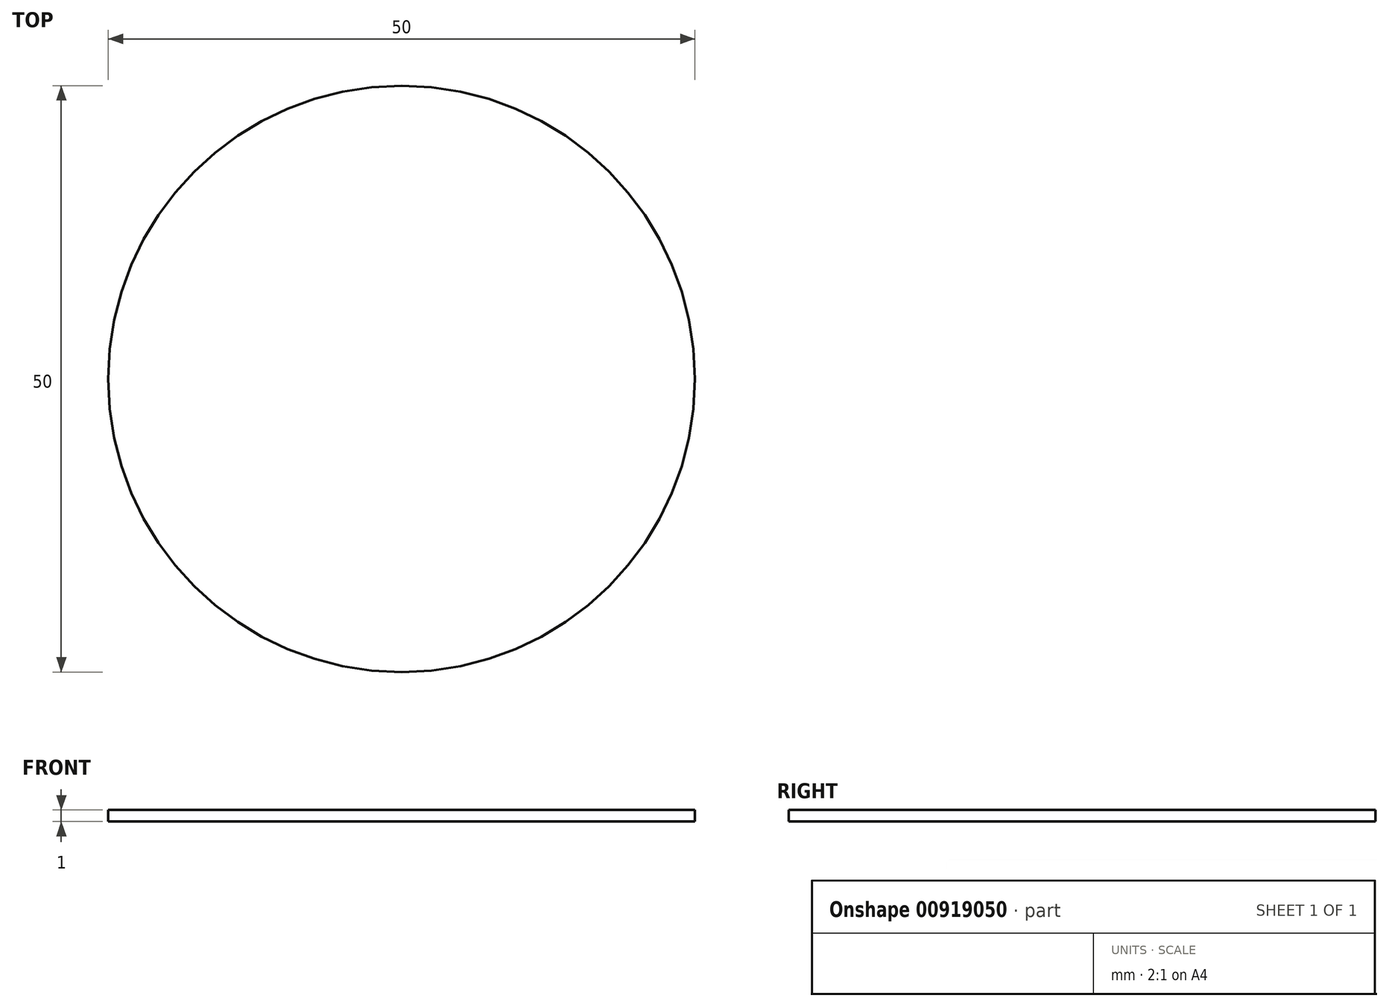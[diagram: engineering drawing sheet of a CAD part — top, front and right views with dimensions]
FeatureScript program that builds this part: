
annotation { "Feature Type Name" : "Feature", "Feature Type Description" : "" }
export const myFeature = defineFeature(function(context is Context, id is Id, definition is map)
    precondition{}
    {
        {
            var Q0;
            Q0=qCreatedBy(makeId("Top.planeOp"),FACE);
            var sketch = newSketch(context, id + "F0", { "sketchPlane" : qUnion([Q0])});
            skCircle(sketch, "E0", {"center": v(0, 0) * mm, "radius": 25 * mm});
            skSolve(sketch);
        }
        {
            var Q0;
            Q0 = qSketchRegion(id + "F0", true);
            extrude(context, id + "F1", {"entities" : qUnion([Q0]), "depth" : 1 * mm, "offsetDistance" : 25 * mm});
        }
    });
